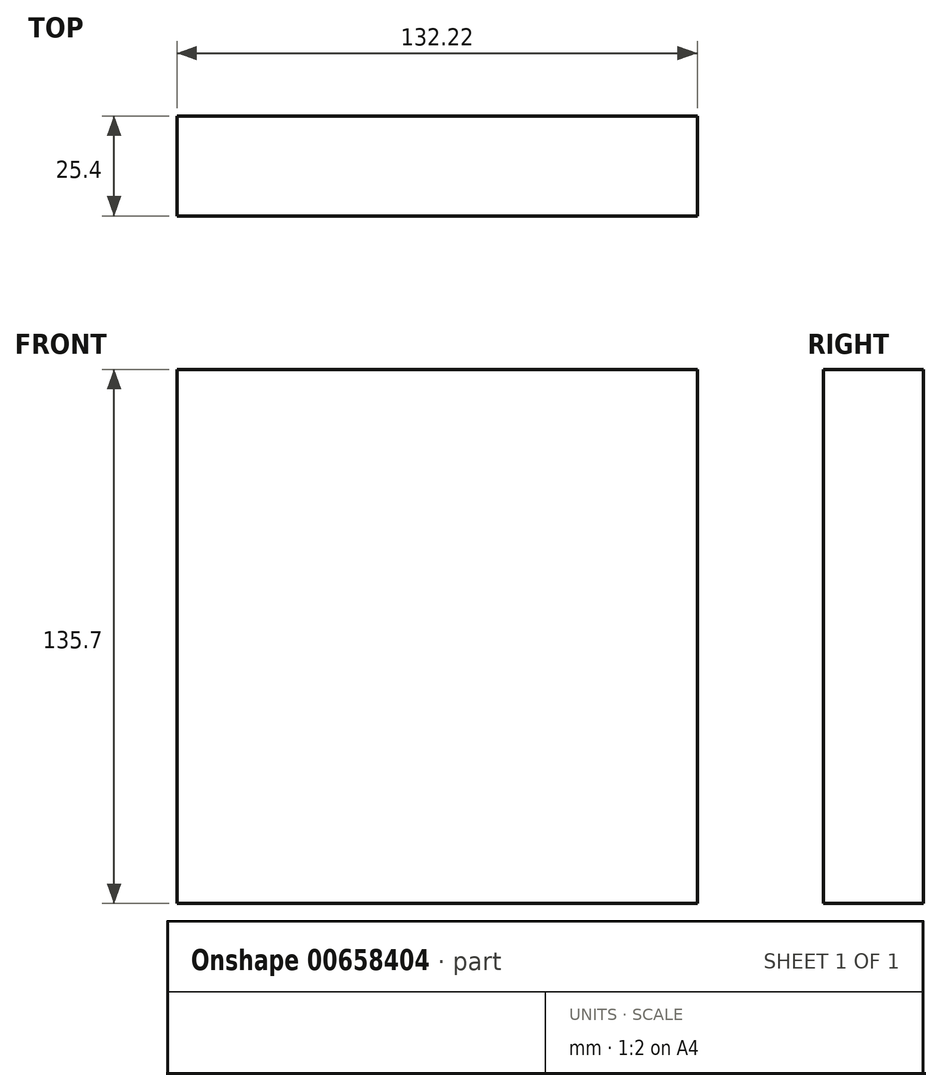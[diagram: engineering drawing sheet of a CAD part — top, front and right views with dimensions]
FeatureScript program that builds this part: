
annotation { "Feature Type Name" : "Feature", "Feature Type Description" : "" }
export const myFeature = defineFeature(function(context is Context, id is Id, definition is map)
    precondition{}
    {
        {
            var Q0;
            Q0=qCreatedBy(makeId("Front.planeOp"),FACE);
            var sketch = newSketch(context, id + "F0", { "sketchPlane" : qUnion([Q0])});
            skLineSegment(sketch, "E0.bottom", {"start": v(-63.36, 65.37) * mm, "end": v(68.86, 65.37) * mm});
            skLineSegment(sketch, "E0.top", {"start": v(-63.36, -70.33) * mm, "end": v(68.86, -70.33) * mm});
            skLineSegment(sketch, "E0.left", {"start": v(-63.36, 65.37) * mm, "end": v(-63.36, -70.33) * mm});
            skLineSegment(sketch, "E0.right", {"start": v(68.86, 65.37) * mm, "end": v(68.86, -70.33) * mm});
            skSolve(sketch);
        }
        {
            var Q0;
            Q0 = qSketchRegion(id + "F0", true);
            extrude(context, id + "F1", {"entities" : qUnion([Q0]), "depth" : 25.4 * mm, "offsetDistance" : 25.4 * mm});
        }
    });
